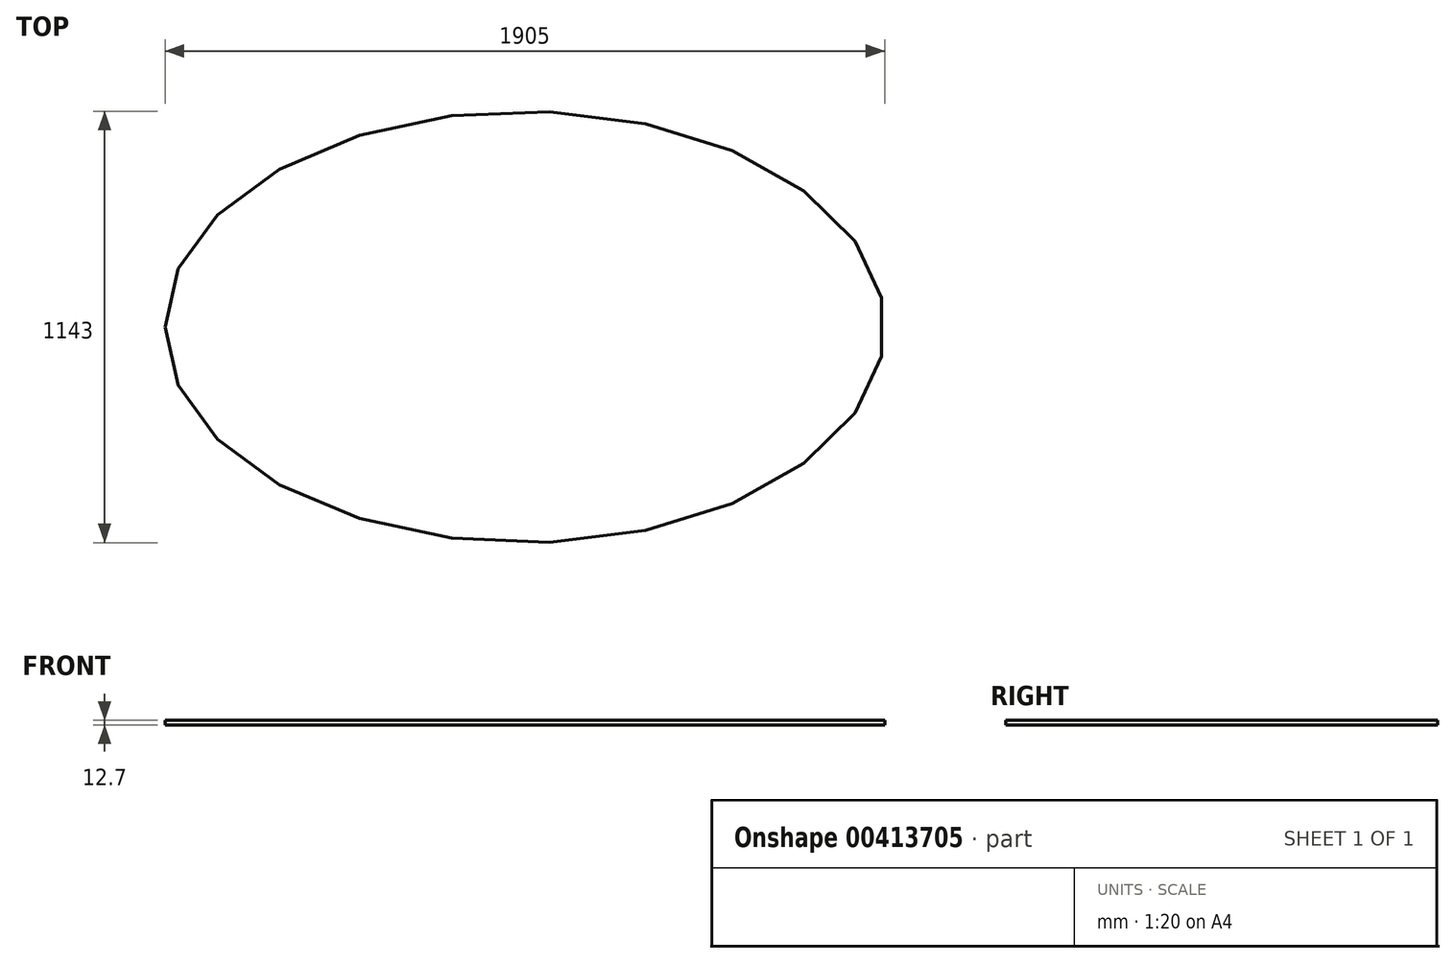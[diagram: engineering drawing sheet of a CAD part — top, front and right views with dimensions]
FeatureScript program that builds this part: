
annotation { "Feature Type Name" : "Feature", "Feature Type Description" : "" }
export const myFeature = defineFeature(function(context is Context, id is Id, definition is map)
    precondition{}
    {
        {
            var Q0;
            Q0=qCreatedBy(makeId("Top.planeOp"),FACE);
            var sketch = newSketch(context, id + "F0", { "sketchPlane" : qUnion([Q0])});
            skEllipse(sketch, "E0", {"center": v(0, 0) * mm, "majorRadius": 952.5 * mm, "minorRadius": 571.5 * mm, "majorAxis": v(-1, 0)});
            skSolve(sketch);
        }
        {
            var Q0;
            Q0 = qSketchRegion(id + "F0", true);
            extrude(context, id + "F1", {"entities" : qUnion([Q0]), "depth" : 12.7 * mm});
        }
    });
